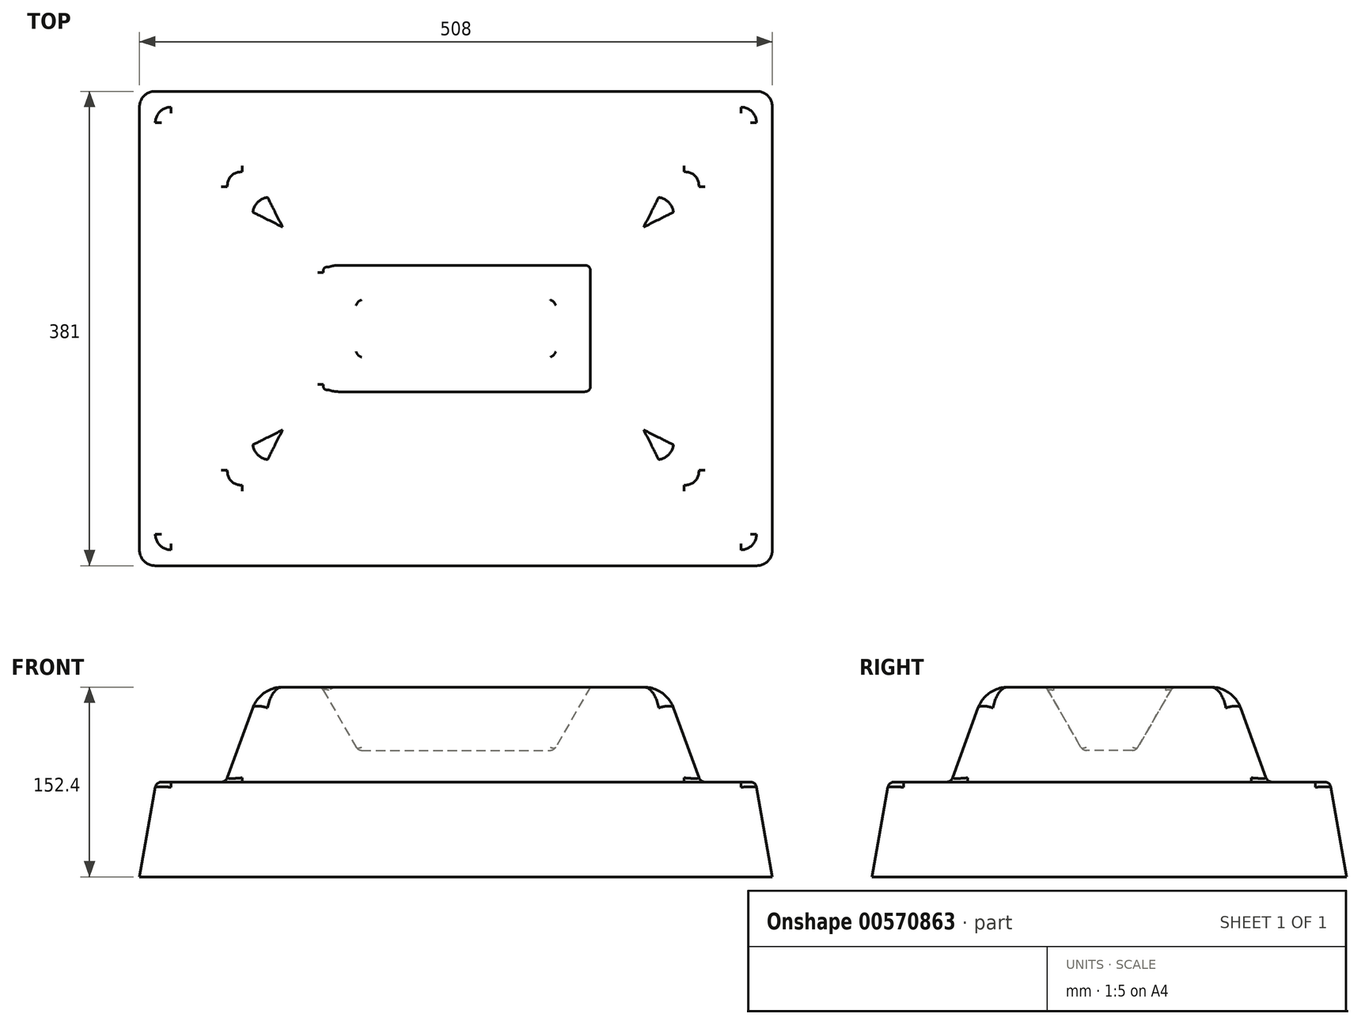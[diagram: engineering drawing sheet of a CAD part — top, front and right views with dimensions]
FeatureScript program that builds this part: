
annotation { "Feature Type Name" : "Feature", "Feature Type Description" : "" }
export const myFeature = defineFeature(function(context is Context, id is Id, definition is map)
    precondition{}
    {
        {
            var Q0;
            Q0=qCreatedBy(makeId("Top.planeOp"),FACE);
            var sketch = newSketch(context, id + "F0", { "sketchPlane" : qUnion([Q0])});
            skLineSegment(sketch, "E0.bottom", {"start": v(254, 190.5) * mm, "end": v(-254, 190.5) * mm});
            skLineSegment(sketch, "E0.top", {"start": v(254, -190.5) * mm, "end": v(-254, -190.5) * mm});
            skLineSegment(sketch, "E0.left", {"start": v(254, 190.5) * mm, "end": v(254, -190.5) * mm});
            skLineSegment(sketch, "E0.right", {"start": v(-254, 190.5) * mm, "end": v(-254, -190.5) * mm});
            skPoint(sketch, "E0.middle", {"position": v(0, 0) * mm});
            skSolve(sketch);
        }
        {
            var Q0;
            Q0 = qSketchRegion(id + "F0", true);
            extrude(context, id + "F1", {"entities" : qUnion([Q0]), "depth" : 76.2 * mm, "offsetDistance" : 25.4 * mm, "hasDraft" : true, "draftAngle" : 10 * degree, "draftPullDirection" : true});
        }
        {
            var Q0;
            Q0=makeQuery(id+"F1.opExtrude","CAP_FACE",FACE,{"disambiguationData":[OSD([sQuery(id+"F0.wireOp",EDGE,"E0.bottom"),sQuery(id+"F0.wireOp",EDGE,"E0.top"),sQuery(id+"F0.wireOp",EDGE,"E0.left"),sQuery(id+"F0.wireOp",EDGE,"E0.right")])],"isStart":false});
            var sketch = newSketch(context, id + "F2", { "sketchPlane" : qUnion([Q0])});
            skLineSegment(sketch, "E1.bottom", {"start": v(196.29, 127) * mm, "end": v(-184.71, 127) * mm});
            skLineSegment(sketch, "E1.top", {"start": v(196.29, -127) * mm, "end": v(-184.71, -127) * mm});
            skLineSegment(sketch, "E1.left", {"start": v(196.29, 127) * mm, "end": v(196.29, -127) * mm});
            skLineSegment(sketch, "E1.right", {"start": v(-184.71, 127) * mm, "end": v(-184.71, -127) * mm});
            skPoint(sketch, "E1.middle", {"position": v(5.79, 0) * mm});
            skSolve(sketch);
        }
        {
            var Q0;
            Q0=makeQuery(id+"F2.imprint","IMPRINT",FACE,{"disambiguationData":[TD([[makeQuery(id+"F2.imprint","IMPRINT",EDGE,{"derivedFrom":sQuery(id+"F2.wireOp",EDGE,"E1.bottom")}),1.0]])]});
            extrude(context, id + "F3", {"entities" : qUnion([Q0]), "operationType" : NewBodyOperationType.ADD, "depth" : 76.2 * mm, "offsetDistance" : 25.4 * mm, "hasDraft" : true, "draftAngle" : 20 * degree, "draftPullDirection" : true});
        }
        {
            var Q0;
            Q0=makeQuery(id+"F3.opExtrude","SWEPT_EDGE",EDGE,{"disambiguationData":[OSD([sQuery(id+"F2.wireOp",EDGE,"E1.bottom"),sQuery(id+"F2.wireOp",EDGE,"E1.right")])]});
            var Q1;
            Q1=makeQuery(id+"F3.opExtrude","SWEPT_EDGE",EDGE,{"disambiguationData":[OSD([sQuery(id+"F2.wireOp",EDGE,"E1.bottom"),sQuery(id+"F2.wireOp",EDGE,"E1.left")])]});
            var Q2;
            Q2=makeQuery(id+"F3.opExtrude","SWEPT_EDGE",EDGE,{"disambiguationData":[OSD([sQuery(id+"F2.wireOp",EDGE,"E1.top"),sQuery(id+"F2.wireOp",EDGE,"E1.left")])]});
            var Q3;
            Q3=makeQuery(id+"F3.opExtrude","SWEPT_EDGE",EDGE,{"disambiguationData":[OSD([sQuery(id+"F2.wireOp",EDGE,"E1.top"),sQuery(id+"F2.wireOp",EDGE,"E1.right")])]});
            var Q4;
            Q4=makeQuery(id+"F1.opExtrude","SWEPT_EDGE",EDGE,{"disambiguationData":[OSD([sQuery(id+"F0.wireOp",EDGE,"E0.bottom"),sQuery(id+"F0.wireOp",EDGE,"E0.left")])]});
            var Q5;
            Q5=makeQuery(id+"F1.opExtrude","SWEPT_EDGE",EDGE,{"disambiguationData":[OSD([sQuery(id+"F0.wireOp",EDGE,"E0.bottom"),sQuery(id+"F0.wireOp",EDGE,"E0.right")])]});
            var Q6;
            Q6=makeQuery(id+"F1.opExtrude","SWEPT_EDGE",EDGE,{"disambiguationData":[OSD([sQuery(id+"F0.wireOp",EDGE,"E0.top"),sQuery(id+"F0.wireOp",EDGE,"E0.right")])]});
            var Q7;
            Q7=makeQuery(id+"F1.opExtrude","SWEPT_EDGE",EDGE,{"disambiguationData":[OSD([sQuery(id+"F0.wireOp",EDGE,"E0.top"),sQuery(id+"F0.wireOp",EDGE,"E0.left")])]});
            fillet(context, id + "F4", {"entities" : qUnion([Q0, Q1, Q2, Q3, Q4, Q5, Q6, Q7]), "radius" : 12.7 * mm, "tangentPropagation" : true, "allowEdgeOverflow" : false});
        }
        {
            var Q0;
            Q0=makeQuery(id+"F3.opExtrude","CAP_EDGE",EDGE,{"disambiguationData":[OSD([sQuery(id+"F2.wireOp",EDGE,"E1.right")])],"isStart":true});
            var Q1;
            Q1=makeQuery(id+"F3.opExtrude","CAP_EDGE",EDGE,{"disambiguationData":[OSD([sQuery(id+"F2.wireOp",EDGE,"E1.bottom")])],"isStart":true});
            var Q2;
            Q2=makeQuery(id+"F1.opExtrude","CAP_FACE",FACE,{"disambiguationData":[OSD([sQuery(id+"F0.wireOp",EDGE,"E0.bottom"),sQuery(id+"F0.wireOp",EDGE,"E0.top"),sQuery(id+"F0.wireOp",EDGE,"E0.left"),sQuery(id+"F0.wireOp",EDGE,"E0.right")])],"isStart":false});
            fillet(context, id + "F5", {"entities" : qUnion([Q0, Q1, Q2]), "radius" : 5.08 * mm, "tangentPropagation" : true, "allowEdgeOverflow" : false});
        }
        {
            var Q0;
            Q0=makeQuery(id+"F3.opExtrude","CAP_FACE",FACE,{"disambiguationData":[OSD([sQuery(id+"F2.wireOp",EDGE,"E1.bottom"),sQuery(id+"F2.wireOp",EDGE,"E1.top"),sQuery(id+"F2.wireOp",EDGE,"E1.left"),sQuery(id+"F2.wireOp",EDGE,"E1.right")])],"isStart":false});
            fillet(context, id + "F6", {"entities" : qUnion([Q0]), "radius" : 25.4 * mm, "tangentPropagation" : true, "allowEdgeOverflow" : false});
        }
        {
            var Q0;
            Q0=makeQuery(id+"F3.opExtrude","CAP_FACE",FACE,{"disambiguationData":[OSD([sQuery(id+"F2.wireOp",EDGE,"E1.bottom"),sQuery(id+"F2.wireOp",EDGE,"E1.top"),sQuery(id+"F2.wireOp",EDGE,"E1.left"),sQuery(id+"F2.wireOp",EDGE,"E1.right")])],"isStart":false});
            var sketch = newSketch(context, id + "F7", { "sketchPlane" : qUnion([Q0])});
            skLineSegment(sketch, "E2.bottom", {"start": v(107.95, 50.8) * mm, "end": v(-107.95, 50.8) * mm});
            skLineSegment(sketch, "E2.top", {"start": v(107.95, -50.8) * mm, "end": v(-107.95, -50.8) * mm});
            skLineSegment(sketch, "E2.left", {"start": v(107.95, 50.8) * mm, "end": v(107.95, -50.8) * mm});
            skLineSegment(sketch, "E2.right", {"start": v(-107.95, 50.8) * mm, "end": v(-107.95, -50.8) * mm});
            skPoint(sketch, "E2.middle", {"position": v(0, 0) * mm});
            skSolve(sketch);
        }
        {
            var Q0;
            Q0=makeQuery(id+"F7.imprint","IMPRINT",FACE,{"disambiguationData":[TD([[makeQuery(id+"F7.imprint","IMPRINT",EDGE,{"derivedFrom":sQuery(id+"F7.wireOp",EDGE,"E2.bottom")}),1.0]])]});
            extrude(context, id + "F8", {"entities" : qUnion([Q0]), "operationType" : NewBodyOperationType.REMOVE, "oppositeDirection" : true, "depth" : 50.8 * mm, "offsetDistance" : 25.4 * mm, "hasDraft" : true, "draftAngle" : 30 * degree, "draftPullDirection" : true});
        }
        {
            var Q0;
            Q0=makeQuery(id+"F8.boolean.opBoolean","COPY",EDGE,{"derivedFrom":makeQuery(id+"F8.opExtrude","SWEPT_EDGE",EDGE,{"disambiguationData":[OSD([sQuery(id+"F7.wireOp",EDGE,"E2.bottom"),sQuery(id+"F7.wireOp",EDGE,"E2.right")])]})});
            var Q1;
            Q1=makeQuery(id+"F8.boolean.opBoolean","COPY",EDGE,{"derivedFrom":makeQuery(id+"F8.opExtrude","SWEPT_EDGE",EDGE,{"disambiguationData":[OSD([sQuery(id+"F7.wireOp",EDGE,"E2.bottom"),sQuery(id+"F7.wireOp",EDGE,"E2.left")])]})});
            var Q2;
            Q2=makeQuery(id+"F8.boolean.opBoolean","COPY",EDGE,{"derivedFrom":makeQuery(id+"F8.opExtrude","SWEPT_EDGE",EDGE,{"disambiguationData":[OSD([sQuery(id+"F7.wireOp",EDGE,"E2.top"),sQuery(id+"F7.wireOp",EDGE,"E2.left")])]})});
            var Q3;
            Q3=makeQuery(id+"F8.boolean.opBoolean","COPY",EDGE,{"derivedFrom":makeQuery(id+"F8.opExtrude","SWEPT_EDGE",EDGE,{"disambiguationData":[OSD([sQuery(id+"F7.wireOp",EDGE,"E2.top"),sQuery(id+"F7.wireOp",EDGE,"E2.right")])]})});
            var Q4;
            Q4=makeQuery(id+"F8.boolean.opBoolean","COPY",FACE,{"derivedFrom":makeQuery(id+"F8.opExtrude","CAP_FACE",FACE,{"disambiguationData":[OSD([sQuery(id+"F7.wireOp",EDGE,"E2.bottom"),sQuery(id+"F7.wireOp",EDGE,"E2.top"),sQuery(id+"F7.wireOp",EDGE,"E2.left"),sQuery(id+"F7.wireOp",EDGE,"E2.right")])],"isStart":false})});
            var Q5;
            Q5=makeQuery(id+"F8.boolean.opBoolean","COPY",FACE,{"derivedFrom":makeQuery(id+"F8.opExtrude","SWEPT_FACE",FACE,{"disambiguationData":[OSD([sQuery(id+"F7.wireOp",EDGE,"E2.right")])]})});
            var Q6;
            Q6=makeQuery(id+"F8.boolean.opBoolean","COPY",EDGE,{"derivedFrom":makeQuery(id+"F8.opExtrude","CAP_EDGE",EDGE,{"disambiguationData":[OSD([sQuery(id+"F7.wireOp",EDGE,"E2.bottom")])],"isStart":true})});
            var Q7;
            Q7=makeQuery(id+"F8.boolean.opBoolean","COPY",EDGE,{"derivedFrom":makeQuery(id+"F8.opExtrude","CAP_EDGE",EDGE,{"disambiguationData":[OSD([sQuery(id+"F7.wireOp",EDGE,"E2.left")])],"isStart":true})});
            var Q8;
            Q8=makeQuery(id+"F8.boolean.opBoolean","COPY",EDGE,{"derivedFrom":makeQuery(id+"F8.opExtrude","CAP_EDGE",EDGE,{"disambiguationData":[OSD([sQuery(id+"F7.wireOp",EDGE,"E2.top")])],"isStart":true})});
            fillet(context, id + "F9", {"entities" : qUnion([Q0, Q1, Q2, Q3, Q4, Q5, Q6, Q7, Q8]), "radius" : 5.08 * mm, "tangentPropagation" : true, "allowEdgeOverflow" : false});
        }
    });
